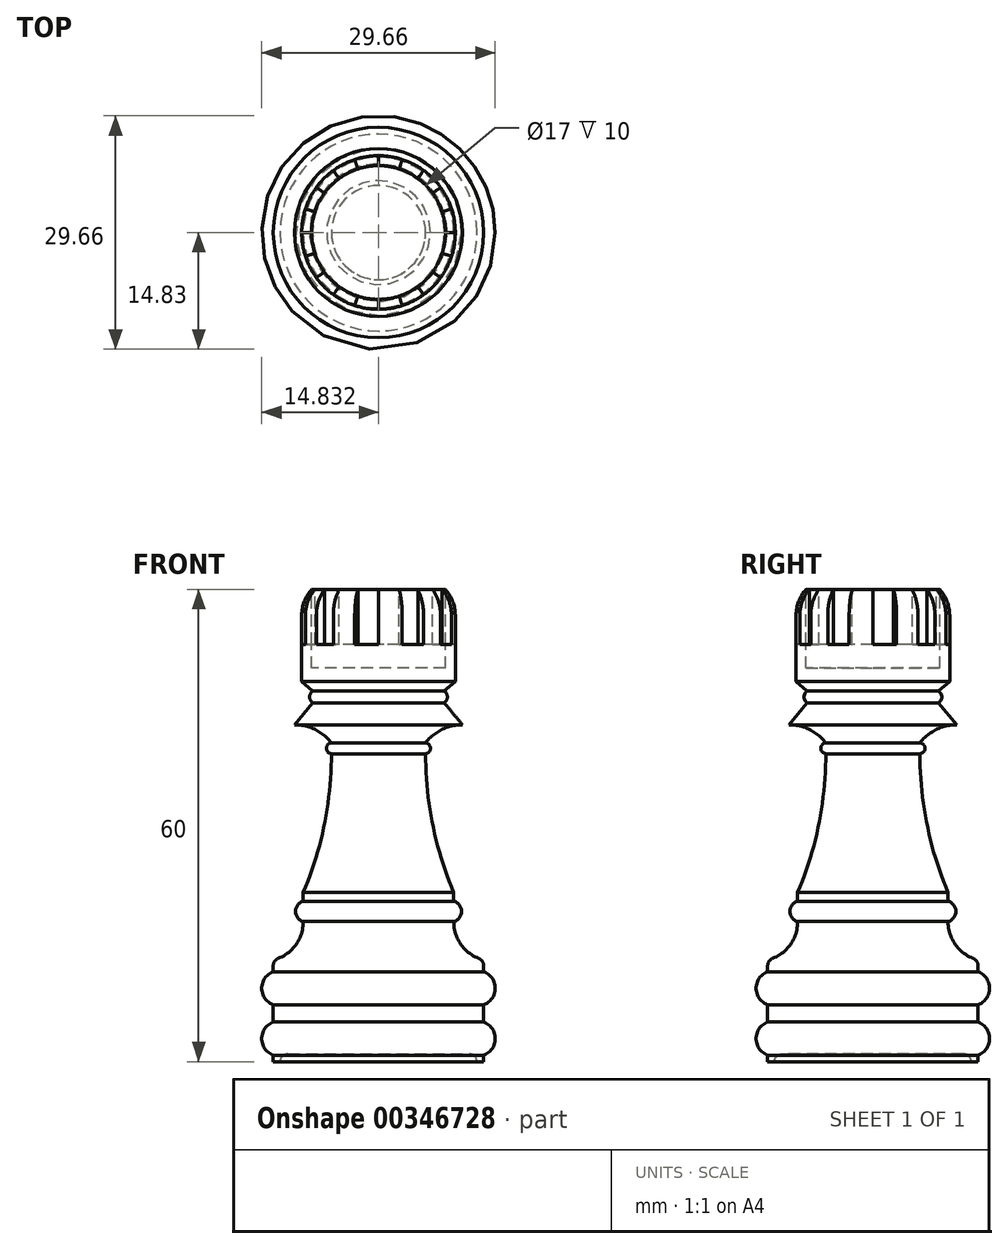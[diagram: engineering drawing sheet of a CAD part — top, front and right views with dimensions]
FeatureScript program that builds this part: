
annotation { "Feature Type Name" : "Feature", "Feature Type Description" : "" }
export const myFeature = defineFeature(function(context is Context, id is Id, definition is map)
    precondition{}
    {
        {
            var Q0;
            Q0=qCreatedBy(makeId("Front.planeOp"),FACE);
            var sketch = newSketch(context, id + "F0", { "sketchPlane" : qUnion([Q0])});
            skLineSegment(sketch, "E0", {"start": v(-21.34, 73.38) * mm, "end": v(-21.34, 23.38) * mm});
            skLineSegment(sketch, "E1", {"start": v(-21.34, 23.38) * mm, "end": v(-7.97, 23.38) * mm});
            skLineSegment(sketch, "E2", {"start": v(-7.97, 23.38) * mm, "end": v(-7.97, 24.21) * mm});
            skLineSegment(sketch, "E3", {"start": v(-7.97, 36.57) * mm, "end": v(-11.78, 36.57) * mm});
            skLineSegment(sketch, "E4", {"start": v(-11.78, 36.57) * mm, "end": v(-11.78, 41.18) * mm});
            skArc(sketch, "E5", {"start": v(-11.78, 41.18) * mm, "mid": v(-10.8, 42.47) * mm, "end": v(-11.78, 43.77) * mm});
            skLineSegment(sketch, "E6", {"start": v(-11.78, 43.77) * mm, "end": v(-11.78, 44.85) * mm});
            skLineSegment(sketch, "E7", {"start": v(-11.78, 44.85) * mm, "end": v(-15.36, 44.85) * mm});
            skLineSegment(sketch, "E8", {"start": v(-15.36, 44.85) * mm, "end": v(-15.36, 62.5) * mm});
            skArc(sketch, "E9", {"start": v(-15.36, 62.5) * mm, "mid": v(-14.73, 63.2) * mm, "end": v(-15.36, 63.9) * mm});
            skLineSegment(sketch, "E10", {"start": v(-15.36, 63.9) * mm, "end": v(-15.36, 66.18) * mm});
            skLineSegment(sketch, "E11", {"start": v(-15.36, 66.18) * mm, "end": v(-10.68, 66.18) * mm});
            skLineSegment(sketch, "E12", {"start": v(-10.68, 66.18) * mm, "end": v(-12.98, 68.96) * mm});
            skArc(sketch, "E13", {"start": v(-12.98, 68.96) * mm, "mid": v(-12.59, 69.72) * mm, "end": v(-12.98, 70.47) * mm});
            skLineSegment(sketch, "E14", {"start": v(-12.98, 70.47) * mm, "end": v(-11.58, 71.68) * mm});
            skLineSegment(sketch, "E15", {"start": v(-11.58, 71.68) * mm, "end": v(-11.58, 73.38) * mm});
            skArc(sketch, "E16", {"start": v(-7.97, 30.6) * mm, "mid": v(-6.5, 32.7) * mm, "end": v(-7.97, 34.8) * mm});
            skLineSegment(sketch, "E17", {"start": v(-7.97, 36.57) * mm, "end": v(-7.97, 34.8) * mm});
            skLineSegment(sketch, "E18", {"start": v(-7.97, 34.8) * mm, "end": v(-7.97, 30.6) * mm});
            skLineSegment(sketch, "E19", {"start": v(-7.97, 30.6) * mm, "end": v(-7.97, 28.41) * mm});
            skArc(sketch, "E20", {"start": v(-7.97, 24.21) * mm, "mid": v(-6.5, 26.31) * mm, "end": v(-7.97, 28.41) * mm});
            skLineSegment(sketch, "E21", {"start": v(-7.97, 28.41) * mm, "end": v(-7.97, 24.21) * mm});
            skLineSegment(sketch, "E22.top", {"start": v(-21.34, 83.38) * mm, "end": v(-11.58, 83.38) * mm});
            skLineSegment(sketch, "E22.left", {"start": v(-21.34, 73.38) * mm, "end": v(-21.34, 83.38) * mm});
            skLineSegment(sketch, "E22.right", {"start": v(-11.58, 73.38) * mm, "end": v(-11.58, 83.38) * mm});
            skSolve(sketch);
        }
        {
            var Q0;
            Q0=makeQuery(id+"F0.imprint","IMPRINT",FACE,{"disambiguationData":[TD([[makeQuery(id+"F0.imprint","IMPRINT",EDGE,{"derivedFrom":sQuery(id+"F0.wireOp",EDGE,"E0")}),1.0]])]});
            var Q1;
            Q1=makeQuery(id+"F0.imprint","IMPRINT",FACE,{"disambiguationData":[TD([[makeQuery(id+"F0.imprint","IMPRINT",EDGE,{"derivedFrom":sQuery(id+"F0.wireOp",EDGE,"E16")}),1.0]])]});
            var Q2;
            Q2=makeQuery(id+"F0.imprint","IMPRINT",FACE,{"disambiguationData":[TD([[makeQuery(id+"F0.imprint","IMPRINT",EDGE,{"derivedFrom":sQuery(id+"F0.wireOp",EDGE,"E20")}),1.0]])]});
            var Q3;
            Q3=sQuery(id+"F0.wireOp",EDGE,"E0");
            revolve(context, id + "F1", {"entities" : qUnion([Q0, Q1, Q2]), "axis" : qUnion([Q3]), "revolveType" : RevolveType.FULL});
        }
        {
            var Q0;
            Q0=makeQuery(id+"F1.opRevolve","SWEPT_EDGE",EDGE,{"disambiguationData":[OSD([sQuery(id+"F0.wireOp",EDGE,"E3"),sQuery(id+"F0.wireOp",EDGE,"E17")])]});
            fillet(context, id + "F2", {"entities" : qUnion([Q0]), "radius" : 1 * mm, "tangentPropagation" : true, "allowEdgeOverflow" : false});
        }
        {
            var Q0;
            Q0=makeQuery(id+"F1.opRevolve","SWEPT_EDGE",EDGE,{"disambiguationData":[OSD([sQuery(id+"F0.wireOp",EDGE,"E7"),sQuery(id+"F0.wireOp",EDGE,"E8")])]});
            fillet(context, id + "F3", {"entities" : qUnion([Q0]), "radius" : 45.3 * mm, "tangentPropagation" : true, "allowEdgeOverflow" : false});
        }
        {
            var Q0;
            Q0=makeQuery(id+"F1.opRevolve","SWEPT_EDGE",EDGE,{"disambiguationData":[OSD([sQuery(id+"F0.wireOp",EDGE,"E10"),sQuery(id+"F0.wireOp",EDGE,"E11")])]});
            fillet(context, id + "F4", {"entities" : qUnion([Q0]), "radius" : 5.9 * mm, "tangentPropagation" : true, "allowEdgeOverflow" : false});
        }
        {
            var Q0;
            Q0=makeQuery(id+"F1.opRevolve","SWEPT_FACE",FACE,{"disambiguationData":[OSD([sQuery(id+"F0.wireOp",EDGE,"E22.top")])]});
            var sketch = newSketch(context, id + "F5", { "sketchPlane" : qUnion([Q0])});
            skCircle(sketch, "E23", {"center": v(-21.34, 0) * mm, "radius": 8.5 * mm});
            skLineSegment(sketch, "E24", {"start": v(-21.34, 0) * mm, "end": v(-21.34, -8.5) * mm});
            skLineSegment(sketch, "E25", {"start": v(-21.34, -8.5) * mm, "end": v(-21.34, -9.76) * mm});
            skLineSegment(sketch, "E26", {"start": v(-21.34, 0) * mm, "end": v(-12.84, 0) * mm});
            skLineSegment(sketch, "E27", {"start": v(-12.84, 0) * mm, "end": v(-11.58, 0) * mm});
            skLineSegment(sketch, "E28", {"start": v(-21.34, 0) * mm, "end": v(-21.34, 8.5) * mm});
            skLineSegment(sketch, "E29", {"start": v(-21.34, 8.5) * mm, "end": v(-21.34, 9.76) * mm});
            skLineSegment(sketch, "E30", {"start": v(-21.34, 0) * mm, "end": v(-29.84, 0) * mm});
            skLineSegment(sketch, "E31", {"start": v(-29.84, 0) * mm, "end": v(-31.1, 0) * mm});
            skLineSegment(sketch, "E32", {"start": v(-21.34, 0) * mm, "end": v(-30.62, -3.01) * mm});
            skLineSegment(sketch, "E33", {"start": v(-21.34, 0) * mm, "end": v(-29.23, -5.73) * mm});
            skLineSegment(sketch, "E34", {"start": v(-21.34, 0) * mm, "end": v(-27.07, -7.9) * mm});
            skLineSegment(sketch, "E35", {"start": v(-21.34, 0) * mm, "end": v(-24.35, -9.28) * mm});
            skLineSegment(sketch, "E36", {"start": v(-21.34, 0) * mm, "end": v(-18.32, -9.28) * mm});
            skLineSegment(sketch, "E37", {"start": v(-15.6, -7.9) * mm, "end": v(-21.34, 0) * mm});
            skLineSegment(sketch, "E38", {"start": v(-21.34, 0) * mm, "end": v(-13.45, -5.73) * mm});
            skLineSegment(sketch, "E39", {"start": v(-12.06, -3.01) * mm, "end": v(-21.34, 0) * mm});
            skLineSegment(sketch, "E40", {"start": v(-30.62, 3.01) * mm, "end": v(-21.34, 0) * mm});
            skLineSegment(sketch, "E41", {"start": v(-21.34, 0) * mm, "end": v(-29.23, 5.73) * mm});
            skLineSegment(sketch, "E42", {"start": v(-21.34, 0) * mm, "end": v(-27.07, 7.9) * mm});
            skLineSegment(sketch, "E43", {"start": v(-21.34, 0) * mm, "end": v(-24.35, 9.28) * mm});
            skLineSegment(sketch, "E44", {"start": v(-21.34, 0) * mm, "end": v(-18.32, 9.28) * mm});
            skLineSegment(sketch, "E45", {"start": v(-21.34, 0) * mm, "end": v(-15.6, 7.9) * mm});
            skLineSegment(sketch, "E46", {"start": v(-21.34, 0) * mm, "end": v(-13.45, 5.73) * mm});
            skLineSegment(sketch, "E47", {"start": v(-21.34, 0) * mm, "end": v(-12.06, 3.01) * mm});
            skCircle(sketch, "E48", {"center": v(-21.34, 0) * mm, "radius": 9.76 * mm});
            skSolve(sketch);
        }
        {
            var Q0;
            {var subQ0=sQuery(id+"F5.wireOp",EDGE,"E29");Q0=makeQuery(id+"F5.imprint","IMPRINT",FACE,{"disambiguationData":[TD([[makeQuery(id+"F5.imprint","IMPRINT",EDGE,{"derivedFrom":subQ0}),-1.0]])]});}
            var Q1;
            {var subQ0=sQuery(id+"F5.wireOp",EDGE,"E46");var subQ1=sQuery(id+"F5.wireOp",EDGE,"E23");var subQ2=makeQuery(id+"F5.imprint","INTERSECT",VERTEX,{"derivedFrom":[subQ1,subQ0]});Q1=makeQuery(id+"F5.imprint","IMPRINT",FACE,{"disambiguationData":[TD([[makeQuery(id+"F5.imprint","IMPRINT",EDGE,{"disambiguationData":[TD([[subQ2,-1.0]])],"derivedFrom":subQ1}),-1.0]])]});}
            var Q2;
            {var subQ0=sQuery(id+"F5.wireOp",EDGE,"E27");Q2=makeQuery(id+"F5.imprint","IMPRINT",FACE,{"disambiguationData":[TD([[makeQuery(id+"F5.imprint","IMPRINT",EDGE,{"derivedFrom":subQ0}),1.0]])]});}
            var Q3;
            {var subQ0=sQuery(id+"F5.wireOp",EDGE,"E38");var subQ1=sQuery(id+"F5.wireOp",EDGE,"E23");var subQ2=makeQuery(id+"F5.imprint","INTERSECT",VERTEX,{"derivedFrom":[subQ1,subQ0]});Q3=makeQuery(id+"F5.imprint","IMPRINT",FACE,{"disambiguationData":[TD([[makeQuery(id+"F5.imprint","IMPRINT",EDGE,{"disambiguationData":[TD([[subQ2,-1.0]])],"derivedFrom":subQ1}),-1.0]])]});}
            var Q4;
            {var subQ0=sQuery(id+"F5.wireOp",EDGE,"E36");var subQ1=sQuery(id+"F5.wireOp",EDGE,"E23");var subQ2=makeQuery(id+"F5.imprint","INTERSECT",VERTEX,{"derivedFrom":[subQ1,subQ0]});Q4=makeQuery(id+"F5.imprint","IMPRINT",FACE,{"disambiguationData":[TD([[makeQuery(id+"F5.imprint","IMPRINT",EDGE,{"disambiguationData":[TD([[subQ2,-1.0]])],"derivedFrom":subQ1}),-1.0]])]});}
            var Q5;
            {var subQ0=sQuery(id+"F5.wireOp",EDGE,"E25");Q5=makeQuery(id+"F5.imprint","IMPRINT",FACE,{"disambiguationData":[TD([[makeQuery(id+"F5.imprint","IMPRINT",EDGE,{"derivedFrom":subQ0}),-1.0]])]});}
            var Q6;
            {var subQ0=sQuery(id+"F5.wireOp",EDGE,"E33");var subQ1=sQuery(id+"F5.wireOp",EDGE,"E23");var subQ2=makeQuery(id+"F5.imprint","INTERSECT",VERTEX,{"derivedFrom":[subQ1,subQ0]});Q6=makeQuery(id+"F5.imprint","IMPRINT",FACE,{"disambiguationData":[TD([[makeQuery(id+"F5.imprint","IMPRINT",EDGE,{"disambiguationData":[TD([[subQ2,-1.0]])],"derivedFrom":subQ1}),-1.0]])]});}
            var Q7;
            {var subQ0=sQuery(id+"F5.wireOp",EDGE,"E31");Q7=makeQuery(id+"F5.imprint","IMPRINT",FACE,{"disambiguationData":[TD([[makeQuery(id+"F5.imprint","IMPRINT",EDGE,{"derivedFrom":subQ0}),1.0]])]});}
            var Q8;
            {var subQ0=sQuery(id+"F5.wireOp",EDGE,"E41");var subQ1=sQuery(id+"F5.wireOp",EDGE,"E23");var subQ2=makeQuery(id+"F5.imprint","INTERSECT",VERTEX,{"derivedFrom":[subQ1,subQ0]});Q8=makeQuery(id+"F5.imprint","IMPRINT",FACE,{"disambiguationData":[TD([[makeQuery(id+"F5.imprint","IMPRINT",EDGE,{"disambiguationData":[TD([[subQ2,-1.0]])],"derivedFrom":subQ1}),-1.0]])]});}
            var Q9;
            {var subQ0=sQuery(id+"F5.wireOp",EDGE,"E43");var subQ1=sQuery(id+"F5.wireOp",EDGE,"E23");var subQ2=makeQuery(id+"F5.imprint","INTERSECT",VERTEX,{"derivedFrom":[subQ1,subQ0]});Q9=makeQuery(id+"F5.imprint","IMPRINT",FACE,{"disambiguationData":[TD([[makeQuery(id+"F5.imprint","IMPRINT",EDGE,{"disambiguationData":[TD([[subQ2,-1.0]])],"derivedFrom":subQ1}),-1.0]])]});}
            extrude(context, id + "F6", {"entities" : qUnion([Q0, Q1, Q2, Q3, Q4, Q5, Q6, Q7, Q8, Q9]), "operationType" : NewBodyOperationType.REMOVE, "oppositeDirection" : true, "depth" : 7 * mm});
        }
        {
            var Q0;
            {var subQ0=sQuery(id+"F5.wireOp",EDGE,"E32");var subQ1=sQuery(id+"F5.wireOp",EDGE,"E23");var subQ2=makeQuery(id+"F5.imprint","INTERSECT",VERTEX,{"derivedFrom":[subQ1,subQ0]});Q0=makeQuery(id+"F5.imprint","IMPRINT",FACE,{"disambiguationData":[TD([[makeQuery(id+"F5.imprint","IMPRINT",EDGE,{"disambiguationData":[TD([[subQ2,-1.0]])],"derivedFrom":subQ1}),1.0]])]});}
            var Q1;
            {var subQ0=sQuery(id+"F5.wireOp",EDGE,"E34");var subQ1=sQuery(id+"F5.wireOp",EDGE,"E23");var subQ2=makeQuery(id+"F5.imprint","INTERSECT",VERTEX,{"derivedFrom":[subQ1,subQ0]});Q1=makeQuery(id+"F5.imprint","IMPRINT",FACE,{"disambiguationData":[TD([[makeQuery(id+"F5.imprint","IMPRINT",EDGE,{"disambiguationData":[TD([[subQ2,-1.0]])],"derivedFrom":subQ1}),1.0]])]});}
            var Q2;
            {var subQ0=sQuery(id+"F5.wireOp",EDGE,"E24");Q2=makeQuery(id+"F5.imprint","IMPRINT",FACE,{"disambiguationData":[TD([[makeQuery(id+"F5.imprint","IMPRINT",EDGE,{"derivedFrom":subQ0}),1.0]])]});}
            var Q3;
            {var subQ0=sQuery(id+"F5.wireOp",EDGE,"E37");var subQ1=sQuery(id+"F5.wireOp",EDGE,"E23");var subQ2=makeQuery(id+"F5.imprint","INTERSECT",VERTEX,{"derivedFrom":[subQ1,subQ0]});Q3=makeQuery(id+"F5.imprint","IMPRINT",FACE,{"disambiguationData":[TD([[makeQuery(id+"F5.imprint","IMPRINT",EDGE,{"disambiguationData":[TD([[subQ2,-1.0]])],"derivedFrom":subQ1}),1.0]])]});}
            var Q4;
            {var subQ0=sQuery(id+"F5.wireOp",EDGE,"E26");Q4=makeQuery(id+"F5.imprint","IMPRINT",FACE,{"disambiguationData":[TD([[makeQuery(id+"F5.imprint","IMPRINT",EDGE,{"derivedFrom":subQ0}),-1.0]])]});}
            var Q5;
            {var subQ0=sQuery(id+"F5.wireOp",EDGE,"E47");var subQ1=sQuery(id+"F5.wireOp",EDGE,"E23");var subQ2=makeQuery(id+"F5.imprint","INTERSECT",VERTEX,{"derivedFrom":[subQ1,subQ0]});Q5=makeQuery(id+"F5.imprint","IMPRINT",FACE,{"disambiguationData":[TD([[makeQuery(id+"F5.imprint","IMPRINT",EDGE,{"disambiguationData":[TD([[subQ2,-1.0]])],"derivedFrom":subQ1}),1.0]])]});}
            var Q6;
            {var subQ0=sQuery(id+"F5.wireOp",EDGE,"E45");var subQ1=sQuery(id+"F5.wireOp",EDGE,"E23");var subQ2=makeQuery(id+"F5.imprint","INTERSECT",VERTEX,{"derivedFrom":[subQ1,subQ0]});Q6=makeQuery(id+"F5.imprint","IMPRINT",FACE,{"disambiguationData":[TD([[makeQuery(id+"F5.imprint","IMPRINT",EDGE,{"disambiguationData":[TD([[subQ2,-1.0]])],"derivedFrom":subQ1}),1.0]])]});}
            var Q7;
            {var subQ0=sQuery(id+"F5.wireOp",EDGE,"E28");Q7=makeQuery(id+"F5.imprint","IMPRINT",FACE,{"disambiguationData":[TD([[makeQuery(id+"F5.imprint","IMPRINT",EDGE,{"derivedFrom":subQ0}),1.0]])]});}
            var Q8;
            {var subQ0=sQuery(id+"F5.wireOp",EDGE,"E42");var subQ1=sQuery(id+"F5.wireOp",EDGE,"E23");var subQ2=makeQuery(id+"F5.imprint","INTERSECT",VERTEX,{"derivedFrom":[subQ1,subQ0]});Q8=makeQuery(id+"F5.imprint","IMPRINT",FACE,{"disambiguationData":[TD([[makeQuery(id+"F5.imprint","IMPRINT",EDGE,{"disambiguationData":[TD([[subQ2,-1.0]])],"derivedFrom":subQ1}),1.0]])]});}
            var Q9;
            {var subQ0=sQuery(id+"F5.wireOp",EDGE,"E30");Q9=makeQuery(id+"F5.imprint","IMPRINT",FACE,{"disambiguationData":[TD([[makeQuery(id+"F5.imprint","IMPRINT",EDGE,{"derivedFrom":subQ0}),-1.0]])]});}
            var Q10;
            {var subQ0=sQuery(id+"F5.wireOp",EDGE,"E24");Q10=makeQuery(id+"F5.imprint","IMPRINT",FACE,{"disambiguationData":[TD([[makeQuery(id+"F5.imprint","IMPRINT",EDGE,{"derivedFrom":subQ0}),-1.0]])]});}
            var Q11;
            {var subQ0=sQuery(id+"F5.wireOp",EDGE,"E33");var subQ1=sQuery(id+"F5.wireOp",EDGE,"E23");var subQ2=makeQuery(id+"F5.imprint","INTERSECT",VERTEX,{"derivedFrom":[subQ1,subQ0]});Q11=makeQuery(id+"F5.imprint","IMPRINT",FACE,{"disambiguationData":[TD([[makeQuery(id+"F5.imprint","IMPRINT",EDGE,{"disambiguationData":[TD([[subQ2,-1.0]])],"derivedFrom":subQ1}),1.0]])]});}
            var Q12;
            {var subQ0=sQuery(id+"F5.wireOp",EDGE,"E30");Q12=makeQuery(id+"F5.imprint","IMPRINT",FACE,{"disambiguationData":[TD([[makeQuery(id+"F5.imprint","IMPRINT",EDGE,{"derivedFrom":subQ0}),1.0]])]});}
            var Q13;
            {var subQ0=sQuery(id+"F5.wireOp",EDGE,"E41");var subQ1=sQuery(id+"F5.wireOp",EDGE,"E23");var subQ2=makeQuery(id+"F5.imprint","INTERSECT",VERTEX,{"derivedFrom":[subQ1,subQ0]});Q13=makeQuery(id+"F5.imprint","IMPRINT",FACE,{"disambiguationData":[TD([[makeQuery(id+"F5.imprint","IMPRINT",EDGE,{"disambiguationData":[TD([[subQ2,-1.0]])],"derivedFrom":subQ1}),1.0]])]});}
            var Q14;
            {var subQ0=sQuery(id+"F5.wireOp",EDGE,"E43");var subQ1=sQuery(id+"F5.wireOp",EDGE,"E23");var subQ2=makeQuery(id+"F5.imprint","INTERSECT",VERTEX,{"derivedFrom":[subQ1,subQ0]});Q14=makeQuery(id+"F5.imprint","IMPRINT",FACE,{"disambiguationData":[TD([[makeQuery(id+"F5.imprint","IMPRINT",EDGE,{"disambiguationData":[TD([[subQ2,-1.0]])],"derivedFrom":subQ1}),1.0]])]});}
            var Q15;
            {var subQ0=sQuery(id+"F5.wireOp",EDGE,"E28");Q15=makeQuery(id+"F5.imprint","IMPRINT",FACE,{"disambiguationData":[TD([[makeQuery(id+"F5.imprint","IMPRINT",EDGE,{"derivedFrom":subQ0}),-1.0]])]});}
            var Q16;
            {var subQ0=sQuery(id+"F5.wireOp",EDGE,"E46");var subQ1=sQuery(id+"F5.wireOp",EDGE,"E23");var subQ2=makeQuery(id+"F5.imprint","INTERSECT",VERTEX,{"derivedFrom":[subQ1,subQ0]});Q16=makeQuery(id+"F5.imprint","IMPRINT",FACE,{"disambiguationData":[TD([[makeQuery(id+"F5.imprint","IMPRINT",EDGE,{"disambiguationData":[TD([[subQ2,-1.0]])],"derivedFrom":subQ1}),1.0]])]});}
            var Q17;
            {var subQ0=sQuery(id+"F5.wireOp",EDGE,"E26");Q17=makeQuery(id+"F5.imprint","IMPRINT",FACE,{"disambiguationData":[TD([[makeQuery(id+"F5.imprint","IMPRINT",EDGE,{"derivedFrom":subQ0}),1.0]])]});}
            var Q18;
            {var subQ0=sQuery(id+"F5.wireOp",EDGE,"E38");var subQ1=sQuery(id+"F5.wireOp",EDGE,"E23");var subQ2=makeQuery(id+"F5.imprint","INTERSECT",VERTEX,{"derivedFrom":[subQ1,subQ0]});Q18=makeQuery(id+"F5.imprint","IMPRINT",FACE,{"disambiguationData":[TD([[makeQuery(id+"F5.imprint","IMPRINT",EDGE,{"disambiguationData":[TD([[subQ2,-1.0]])],"derivedFrom":subQ1}),1.0]])]});}
            var Q19;
            {var subQ0=sQuery(id+"F5.wireOp",EDGE,"E36");var subQ1=sQuery(id+"F5.wireOp",EDGE,"E23");var subQ2=makeQuery(id+"F5.imprint","INTERSECT",VERTEX,{"derivedFrom":[subQ1,subQ0]});Q19=makeQuery(id+"F5.imprint","IMPRINT",FACE,{"disambiguationData":[TD([[makeQuery(id+"F5.imprint","IMPRINT",EDGE,{"disambiguationData":[TD([[subQ2,-1.0]])],"derivedFrom":subQ1}),1.0]])]});}
            extrude(context, id + "F7", {"entities" : qUnion([Q0, Q1, Q2, Q3, Q4, Q5, Q6, Q7, Q8, Q9, Q10, Q11, Q12, Q13, Q14, Q15, Q16, Q17, Q18, Q19]), "operationType" : NewBodyOperationType.REMOVE, "oppositeDirection" : true, "depth" : 10 * mm});
        }
        {
            var Q0;
            {var subQ0=sQuery(id+"F0.wireOp",EDGE,"E22.right");var subQ1=sQuery(id+"F0.wireOp",EDGE,"E22.top");Q0=makeQuery(id+"F6.boolean.opBoolean","SPLIT",EDGE,{"disambiguationData":[TD([makeQuery(id+"F6.opExtrude","SWEPT_FACE",FACE,{"disambiguationData":[OSD([sQuery(id+"F5.wireOp",EDGE,"E32")])]})])],"derivedFrom":makeQuery(id+"F1.opRevolve","SWEPT_EDGE",EDGE,{"disambiguationData":[OSD([subQ1,subQ0])]})});}
            var Q1;
            {var subQ0=sQuery(id+"F0.wireOp",EDGE,"E22.right");var subQ1=sQuery(id+"F0.wireOp",EDGE,"E22.top");Q1=makeQuery(id+"F6.boolean.opBoolean","SPLIT",EDGE,{"disambiguationData":[TD([makeQuery(id+"F6.opExtrude","SWEPT_FACE",FACE,{"disambiguationData":[OSD([sQuery(id+"F5.wireOp",EDGE,"E34")])]})])],"derivedFrom":makeQuery(id+"F1.opRevolve","SWEPT_EDGE",EDGE,{"disambiguationData":[OSD([subQ1,subQ0])]})});}
            var Q2;
            {var subQ0=sQuery(id+"F0.wireOp",EDGE,"E22.right");var subQ1=sQuery(id+"F0.wireOp",EDGE,"E22.top");Q2=makeQuery(id+"F6.boolean.opBoolean","SPLIT",EDGE,{"disambiguationData":[TD([makeQuery(id+"F6.opExtrude","SWEPT_FACE",FACE,{"disambiguationData":[OSD([sQuery(id+"F5.wireOp",EDGE,"E25")])]})])],"derivedFrom":makeQuery(id+"F1.opRevolve","SWEPT_EDGE",EDGE,{"disambiguationData":[OSD([subQ1,subQ0])]})});}
            var Q3;
            {var subQ0=sQuery(id+"F0.wireOp",EDGE,"E22.right");var subQ1=sQuery(id+"F0.wireOp",EDGE,"E22.top");Q3=makeQuery(id+"F6.boolean.opBoolean","SPLIT",EDGE,{"disambiguationData":[TD([makeQuery(id+"F6.opExtrude","SWEPT_FACE",FACE,{"disambiguationData":[OSD([sQuery(id+"F5.wireOp",EDGE,"E37")])]})])],"derivedFrom":makeQuery(id+"F1.opRevolve","SWEPT_EDGE",EDGE,{"disambiguationData":[OSD([subQ1,subQ0])]})});}
            var Q4;
            {var subQ0=sQuery(id+"F0.wireOp",EDGE,"E22.right");var subQ1=sQuery(id+"F0.wireOp",EDGE,"E22.top");Q4=makeQuery(id+"F6.boolean.opBoolean","SPLIT",EDGE,{"disambiguationData":[TD([makeQuery(id+"F6.opExtrude","SWEPT_FACE",FACE,{"disambiguationData":[OSD([sQuery(id+"F5.wireOp",EDGE,"E27")])]})])],"derivedFrom":makeQuery(id+"F1.opRevolve","SWEPT_EDGE",EDGE,{"disambiguationData":[OSD([subQ1,subQ0])]})});}
            var Q5;
            {var subQ0=sQuery(id+"F0.wireOp",EDGE,"E22.right");var subQ1=sQuery(id+"F0.wireOp",EDGE,"E22.top");Q5=makeQuery(id+"F6.boolean.opBoolean","SPLIT",EDGE,{"disambiguationData":[TD([makeQuery(id+"F6.opExtrude","SWEPT_FACE",FACE,{"disambiguationData":[OSD([sQuery(id+"F5.wireOp",EDGE,"E46")])]})])],"derivedFrom":makeQuery(id+"F1.opRevolve","SWEPT_EDGE",EDGE,{"disambiguationData":[OSD([subQ1,subQ0])]})});}
            var Q6;
            {var subQ0=sQuery(id+"F0.wireOp",EDGE,"E22.right");var subQ1=sQuery(id+"F0.wireOp",EDGE,"E22.top");Q6=makeQuery(id+"F6.boolean.opBoolean","SPLIT",EDGE,{"disambiguationData":[TD([makeQuery(id+"F6.opExtrude","SWEPT_FACE",FACE,{"disambiguationData":[OSD([sQuery(id+"F5.wireOp",EDGE,"E44")])]})])],"derivedFrom":makeQuery(id+"F1.opRevolve","SWEPT_EDGE",EDGE,{"disambiguationData":[OSD([subQ1,subQ0])]})});}
            var Q7;
            {var subQ0=sQuery(id+"F0.wireOp",EDGE,"E22.right");var subQ1=sQuery(id+"F0.wireOp",EDGE,"E22.top");Q7=makeQuery(id+"F6.boolean.opBoolean","SPLIT",EDGE,{"disambiguationData":[TD([makeQuery(id+"F6.opExtrude","SWEPT_FACE",FACE,{"disambiguationData":[OSD([sQuery(id+"F5.wireOp",EDGE,"E29")])]})])],"derivedFrom":makeQuery(id+"F1.opRevolve","SWEPT_EDGE",EDGE,{"disambiguationData":[OSD([subQ1,subQ0])]})});}
            var Q8;
            {var subQ0=sQuery(id+"F0.wireOp",EDGE,"E22.right");var subQ1=sQuery(id+"F0.wireOp",EDGE,"E22.top");Q8=makeQuery(id+"F6.boolean.opBoolean","SPLIT",EDGE,{"disambiguationData":[TD([makeQuery(id+"F6.opExtrude","SWEPT_FACE",FACE,{"disambiguationData":[OSD([sQuery(id+"F5.wireOp",EDGE,"E41")])]})])],"derivedFrom":makeQuery(id+"F1.opRevolve","SWEPT_EDGE",EDGE,{"disambiguationData":[OSD([subQ1,subQ0])]})});}
            var Q9;
            {var subQ0=sQuery(id+"F0.wireOp",EDGE,"E22.right");var subQ1=sQuery(id+"F0.wireOp",EDGE,"E22.top");Q9=makeQuery(id+"F6.boolean.opBoolean","SPLIT",EDGE,{"disambiguationData":[TD([makeQuery(id+"F6.opExtrude","SWEPT_FACE",FACE,{"disambiguationData":[OSD([sQuery(id+"F5.wireOp",EDGE,"E31")])]})])],"derivedFrom":makeQuery(id+"F1.opRevolve","SWEPT_EDGE",EDGE,{"disambiguationData":[OSD([subQ1,subQ0])]})});}
            fillet(context, id + "F8", {"entities" : qUnion([Q0, Q1, Q2, Q3, Q4, Q5, Q6, Q7, Q8, Q9]), "radius" : 5 * mm, "tangentPropagation" : true, "allowEdgeOverflow" : false});
        }
        {
            var Q0;
            Q0=makeQuery(id+"F1.opRevolve","SWEPT_FACE",FACE,{"disambiguationData":[OSD([sQuery(id+"F0.wireOp",EDGE,"E1")])]});
            var sketch = newSketch(context, id + "F9", { "sketchPlane" : qUnion([Q0])});
            skCircle(sketch, "E49", {"center": v(-21.34, 0) * mm, "radius": 12.5 * mm});
            skSolve(sketch);
        }
        {
            var Q0;
            Q0=makeQuery(id+"F9.imprint","IMPRINT",FACE,{"disambiguationData":[TD([[makeQuery(id+"F9.imprint","IMPRINT",EDGE,{"derivedFrom":sQuery(id+"F9.wireOp",EDGE,"E49")}),1.0]])]});
            extrude(context, id + "F10", {"entities" : qUnion([Q0]), "operationType" : NewBodyOperationType.REMOVE, "oppositeDirection" : true, "depth" : 1 * mm});
        }
        {
            var Q0;
            Q0=makeQuery(id+"F10.boolean.opBoolean","COPY",EDGE,{"derivedFrom":makeQuery(id+"F10.opExtrude","CAP_EDGE",EDGE,{"disambiguationData":[OSD([sQuery(id+"F9.wireOp",EDGE,"E49")])],"isStart":false})});
            fillet(context, id + "F11", {"entities" : qUnion([Q0]), "radius" : 1 * mm, "tangentPropagation" : true, "allowEdgeOverflow" : false});
        }
        {
            var Q0;
            Q0=makeQuery(id+"F1.opRevolve","SWEPT_EDGE",EDGE,{"disambiguationData":[OSD([sQuery(id+"F0.wireOp",EDGE,"E3"),sQuery(id+"F0.wireOp",EDGE,"E4")])]});
            fillet(context, id + "F12", {"entities" : qUnion([Q0]), "radius" : 5 * mm, "tangentPropagation" : true, "allowEdgeOverflow" : false});
        }
    });
